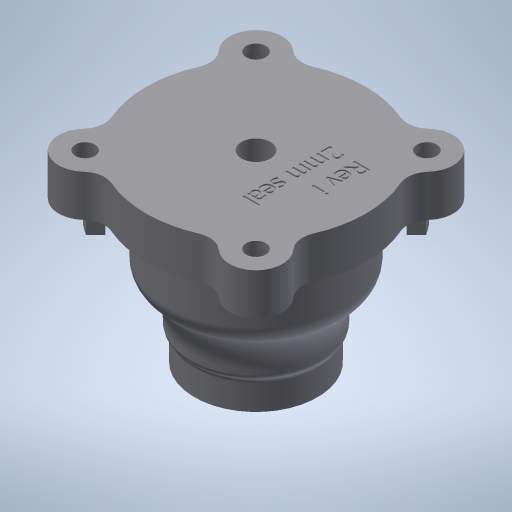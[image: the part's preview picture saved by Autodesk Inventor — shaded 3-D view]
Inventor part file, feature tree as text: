
AUTODESK INVENTOR PART (.ipt)
format: ipt  version: 2023.3 (Build 273359000, 359)  size: 1,084,928 bytes
history: native  units: mm
features: sketch x6, other x3, hole x3, extrude x2, fillet x2, revolve x1, boolean_combine x1, pattern_circular x1, emboss x1, chamfer x1
ambient origin geometry x8: Origin, YZ Plane, XZ Plane, XY Plane, X Axis, Y Axis, Z Axis, Center Point
bodies: Solid1 (feature_tree)
feature tree (21):
  other  "Sealing_ring_20x1_silicone_h.ipt"
  revolve  "Revolution1"  [1 undecoded]
  boolean_combine  "Combine1"
  hole  "Hole1"  [1 undecoded]
  extrude  "Extrusion1"  Depth=1.5mm
  hole  "Hole3"  [1 undecoded]
  fillet  "Fillet2"  Radius=5.0mm
  extrude  "Extrusion2"  Depth=0.3mm
  pattern_circular  "Circular Pattern1"  [2 undecoded]
  emboss  "Emboss1"
  hole  "Hole2"  [1 undecoded]
  fillet  "Fillet1"  Radius=4.5mm
  chamfer  "Chamfer1"  Distance=10.0mm
  other  "TaggingFeature1"
  sketch  "Sketch1"  dims[d0=10.0mm d1=16.75mm]
  other  "Solid1::Sealing_ring_20x1_silicone_h.ipt"
  sketch  "Sketch3"  dims[d5=360.0deg]
  sketch  "Sketch4"  dims[d8=6.6mm d9=3.708mm d10=20.0mm d11=1.5mm d12=90.0deg d13=5.692mm d14=0.0mm d16=0.5mm d17=2.0mm d18=45.0deg]
  sketch  "Sketch5"  dims[d19=2.5mm d23=1.5mm]
  sketch  "Sketch6"  dims[d24=14.0mm d26=1.0mm d28=5.0mm]
  sketch  "Sketch7"  dims[d29=20.0mm d30=6.0mm d31=20.0mm d32=1.5mm d33=14.3117mm d34=20.5mm d35=0.0mm d38=7.0mm d39=5.7mm d52=12.0mm d54=4.5mm d55=10.0mm d56=0.0mm d57=5.7mm d58=6.0mm d59=4.0mm d60=2.0mm d61=90.0deg d62=8.0mm d63=0.0mm d64=5.0mm d65=40.0mm d66=360.0deg d68=45.0deg d69=2.5mm d70=2.0mm d71=20.4mm d73=7.854002mm d76=1.2mm d77=22.8mm d78=3.0mm d79=0.0mm d81=25.0mm d82=28.0mm d83=0.3mm d84=0.0mm d36=0.75mm d37=20.594885mm d40=0.375mm d72=0.5mm]
note: 6 required parameter values undecoded (feature->parameter linkage not recoverable at this tier; creation-order binding heuristic only, values carry confidence <= 0.55)